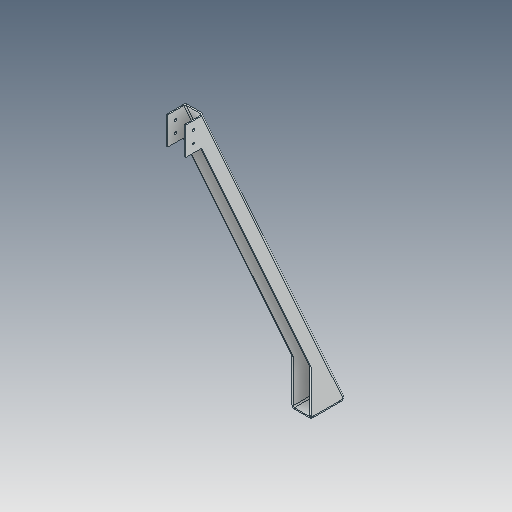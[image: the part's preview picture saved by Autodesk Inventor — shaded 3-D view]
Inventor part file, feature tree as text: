
AUTODESK INVENTOR PART (.ipt)
format: ipt  version: 2023.5 (Build 275446000, 446)  size: 136,704 bytes
history: native  units: in
note: dims shown in document units (in); Inventor stores cm internally (conversion verified against a paired STEP export)
features: fillet x1
ambient origin geometry x8: Origin, YZ Plane, XZ Plane, XY Plane, X Axis, Y Axis, Z Axis, Center Point
bodies: Solid1 (feature_tree)
feature tree (1):
  fillet  "Fillet1"  [1 undecoded]
note: 1 required parameter value undecoded (feature->parameter linkage not recoverable at this tier; creation-order binding heuristic only, values carry confidence <= 0.55)
